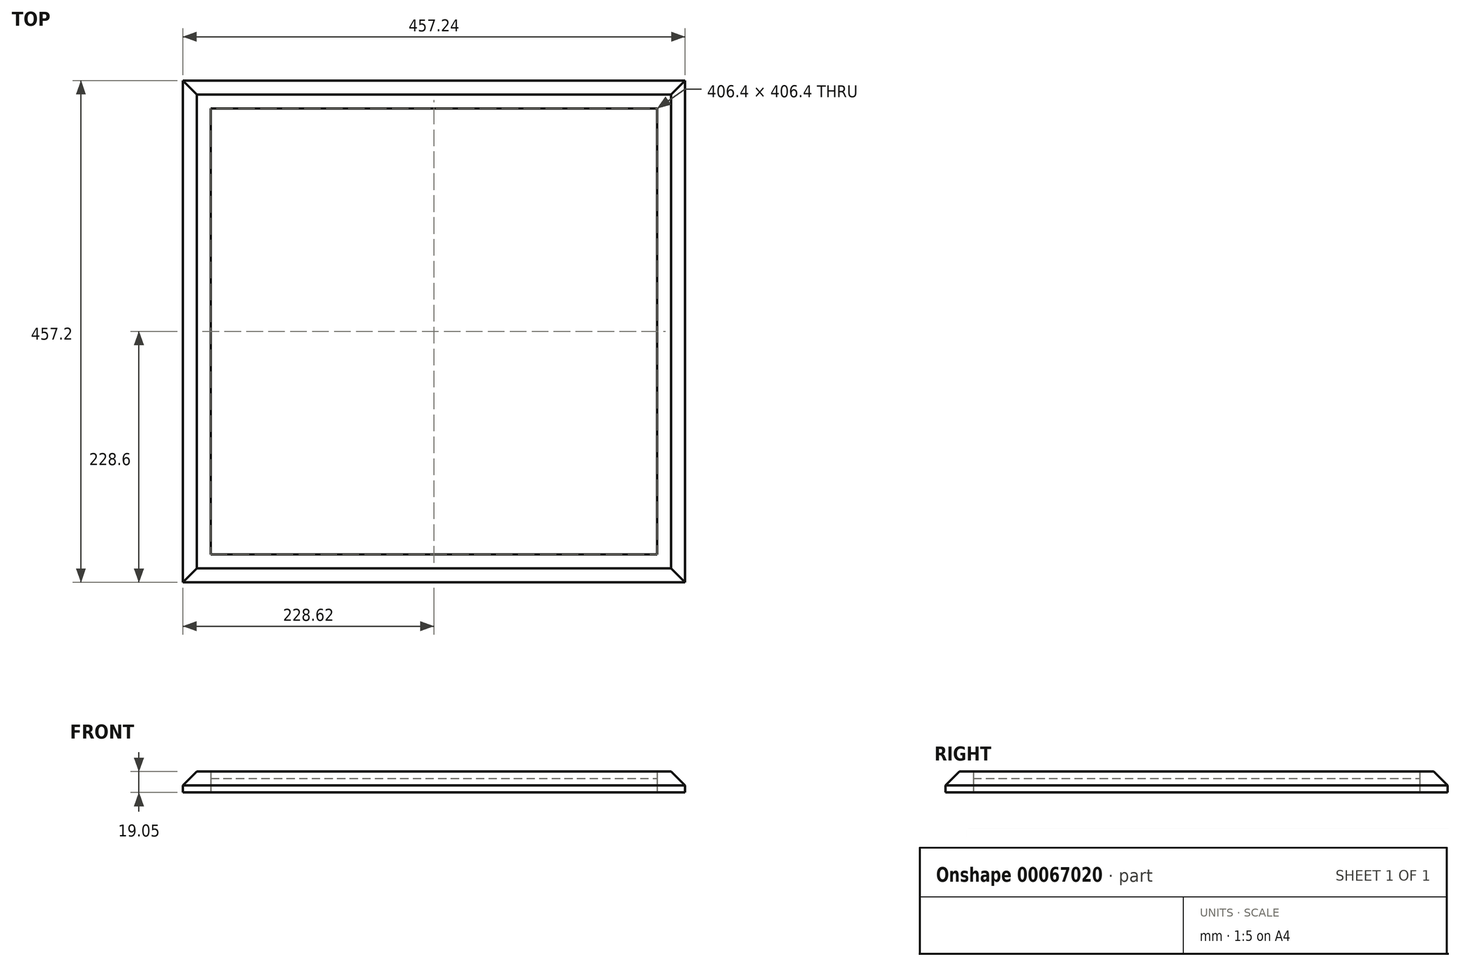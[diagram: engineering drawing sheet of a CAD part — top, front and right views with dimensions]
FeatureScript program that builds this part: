
annotation { "Feature Type Name" : "Feature", "Feature Type Description" : "" }
export const myFeature = defineFeature(function(context is Context, id is Id, definition is map)
    precondition{}
    {
        {
            var Q0;
            Q0=qCreatedBy(makeId("Top.planeOp"),FACE);
            var sketch = newSketch(context, id + "F2", { "sketchPlane" : qUnion([Q0])});
            skLineSegment(sketch, "E0.rect.bottom", {"start": v(-228.62, -228.6) * mm, "end": v(228.62, -228.6) * mm});
            skLineSegment(sketch, "E0.rect.top", {"start": v(-228.62, 228.6) * mm, "end": v(228.62, 228.6) * mm});
            skLineSegment(sketch, "E0.rect.left", {"start": v(-228.62, -228.6) * mm, "end": v(-228.62, 228.6) * mm});
            skLineSegment(sketch, "E0.rect.right", {"start": v(228.62, -228.6) * mm, "end": v(228.62, 228.6) * mm});
            skPoint(sketch, "E0.rect.middle", {"position": v(0, 0) * mm});
            skLineSegment(sketch, "E1.rect.bottom", {"start": v(-203.2, -203.2) * mm, "end": v(203.2, -203.2) * mm});
            skLineSegment(sketch, "E1.rect.top", {"start": v(-203.2, 203.2) * mm, "end": v(203.2, 203.2) * mm});
            skLineSegment(sketch, "E1.rect.left", {"start": v(-203.2, -203.2) * mm, "end": v(-203.2, 203.2) * mm});
            skLineSegment(sketch, "E1.rect.right", {"start": v(203.2, -203.2) * mm, "end": v(203.2, 203.2) * mm});
            skSolve(sketch);
        }
        {
            var Q0;
            Q0=makeQuery(id+"F2.imprint","IMPRINT",FACE,{"disambiguationData":[TD([[makeQuery(id+"F2.imprint","IMPRINT",EDGE,{"derivedFrom":sQuery(id+"F2.wireOp",EDGE,"E0.rect.bottom")}),1.0]])]});
            var sketch = newSketch(context, id + "F0", { "sketchPlane" : qUnion([Q0])});
            skSolve(sketch);
        }
        {
            var Q0;
            Q0 = qSketchRegion(id + "F0", true);
            var Q1;
            Q1=makeQuery(id+"F2.imprint","IMPRINT",FACE,{"disambiguationData":[TD([[makeQuery(id+"F2.imprint","IMPRINT",EDGE,{"derivedFrom":sQuery(id+"F2.wireOp",EDGE,"E1.rect.bottom")}),1.0]])]});
            extrude(context, id + "F3", {"entities" : qUnion([Q0, Q1]), "depth" : 12.7 * mm});
        }
        {
            var Q0;
            Q0 = qSketchRegion(id + "F0", true);
            var Q1;
            Q1=makeQuery(id+"F0.imprint","IMPRINT",FACE,{"disambiguationData":[TD([[makeQuery(id+"F0.imprint","IMPRINT",EDGE,{"derivedFrom":makeQuery(id+"F2.imprint","IMPRINT",EDGE,{"derivedFrom":sQuery(id+"F2.wireOp",EDGE,"E0.rect.bottom")})}),1.0]])]});
            extrude(context, id + "F4", {"entities" : qUnion([Q0, Q1]), "depth" : 19.05 * mm});
        }
        {
            var Q0;
            Q0=makeQuery(id+"F4.opExtrude","CAP_EDGE",EDGE,{"disambiguationData":[OSD([sQuery(id+"F2.wireOp",EDGE,"E0.rect.bottom")])],"isStart":false});
            var Q1;
            Q1=makeQuery(id+"F4.opExtrude","CAP_EDGE",EDGE,{"disambiguationData":[OSD([sQuery(id+"F2.wireOp",EDGE,"E0.rect.left")])],"isStart":false});
            var Q2;
            Q2=makeQuery(id+"F4.opExtrude","CAP_EDGE",EDGE,{"disambiguationData":[OSD([sQuery(id+"F2.wireOp",EDGE,"E0.rect.right")])],"isStart":false});
            var Q3;
            Q3=makeQuery(id+"F4.opExtrude","CAP_EDGE",EDGE,{"disambiguationData":[OSD([sQuery(id+"F2.wireOp",EDGE,"E0.rect.top")])],"isStart":false});
            chamfer(context, id + "F1", {"entities" : qUnion([Q0, Q1, Q2, Q3]), "width" : 12.7 * mm, "tangentPropagation" : true});
        }
    });
